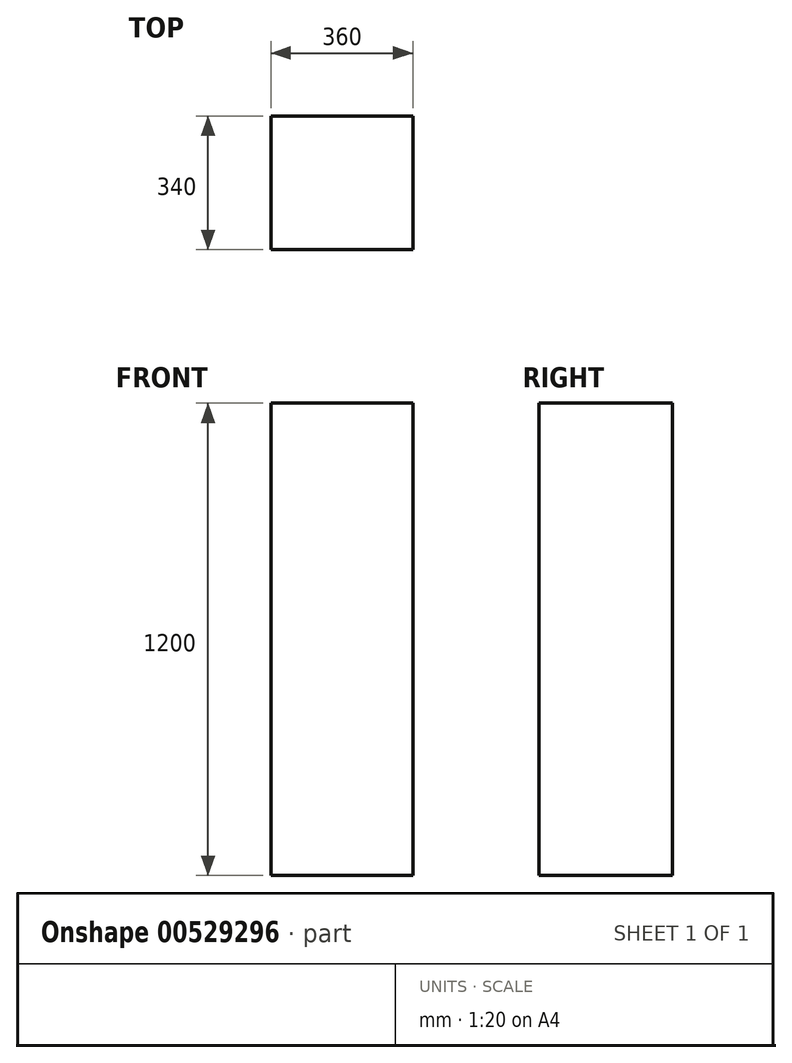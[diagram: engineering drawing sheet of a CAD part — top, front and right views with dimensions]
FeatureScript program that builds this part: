
annotation { "Feature Type Name" : "Feature", "Feature Type Description" : "" }
export const myFeature = defineFeature(function(context is Context, id is Id, definition is map)
    precondition{}
    {
        {
            var Q0;
            Q0=qCreatedBy(makeId("Top.planeOp"),FACE);
            var sketch = newSketch(context, id + "F0", { "sketchPlane" : qUnion([Q0])});
            skLineSegment(sketch, "E0.bottom", {"start": v(-156.3, 198.37) * mm, "end": v(203.7, 198.37) * mm});
            skLineSegment(sketch, "E0.top", {"start": v(-156.3, -141.63) * mm, "end": v(203.7, -141.63) * mm});
            skLineSegment(sketch, "E0.left", {"start": v(-156.3, 198.37) * mm, "end": v(-156.3, -141.63) * mm});
            skLineSegment(sketch, "E0.right", {"start": v(203.7, 198.37) * mm, "end": v(203.7, -141.63) * mm});
            skSolve(sketch);
        }
        {
            var Q0;
            Q0=qSketchRegion(id+"F0",true);
            extrude(context, id + "F1", {"entities" : qUnion([Q0]), "depth" : 1200 * mm, "offsetDistance" : 25 * mm});
        }
    });
